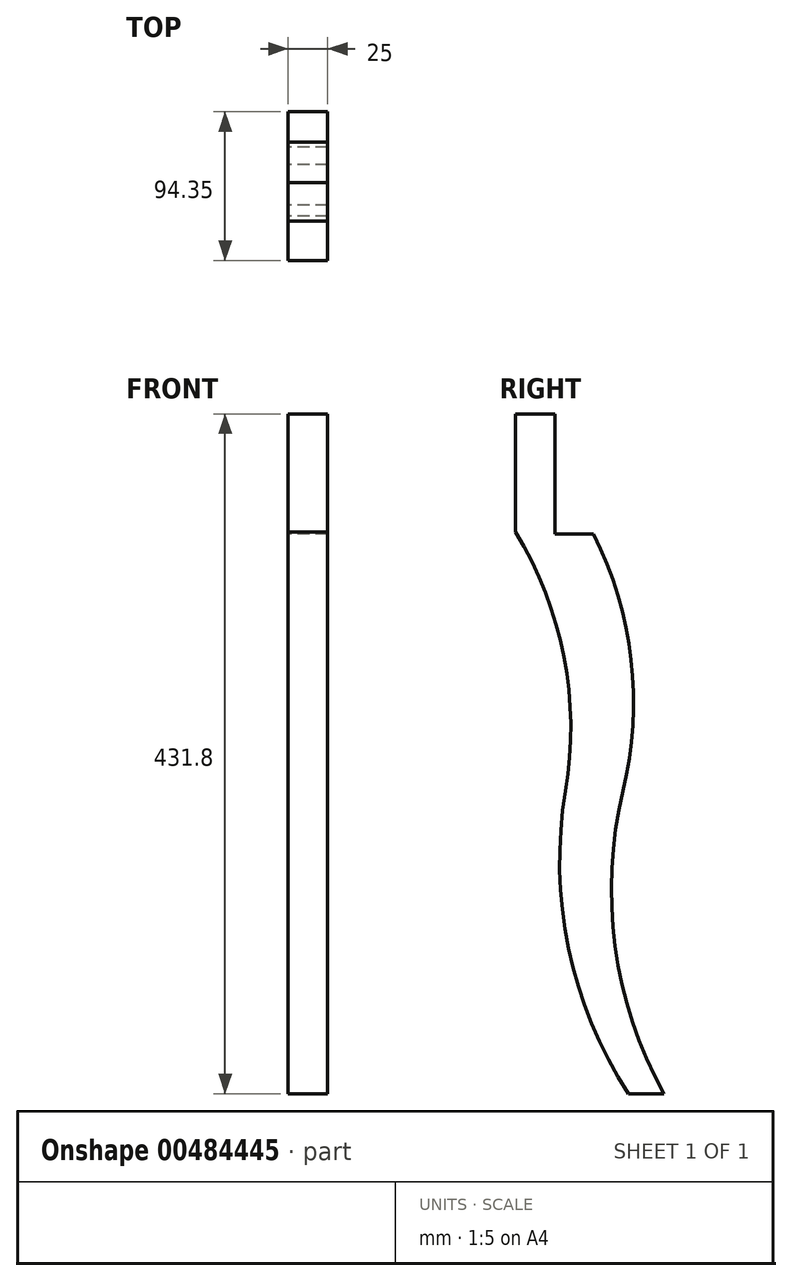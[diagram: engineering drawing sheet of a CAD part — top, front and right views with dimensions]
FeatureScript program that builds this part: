
annotation { "Feature Type Name" : "Feature", "Feature Type Description" : "" }
export const myFeature = defineFeature(function(context is Context, id is Id, definition is map)
    precondition{}
    {
        {
            var Q0;
            Q0=qCreatedBy(makeId("Right.planeOp"),FACE);
            var sketch = newSketch(context, id + "F0", { "sketchPlane" : qUnion([Q0])});
            skLineSegment(sketch, "E0", {"start": v(-61.12, 223.8) * mm, "end": v(-85.62, 223.8) * mm});
            skLineSegment(sketch, "E1", {"start": v(-38.78, -131.8) * mm, "end": v(366.43, -131.8) * mm, "construction": true});
            skLineSegment(sketch, "E2", {"start": v(-256.12, 300) * mm, "end": v(-256.12, -130.22) * mm, "construction": true});
            skLineSegment(sketch, "E3", {"start": v(-85.62, 223.8) * mm, "end": v(-85.62, 300) * mm});
            skLineSegment(sketch, "E4", {"start": v(-85.62, 300) * mm, "end": v(-110.62, 300) * mm});
            skLineSegment(sketch, "E5", {"start": v(-110.62, 300) * mm, "end": v(-110.62, 225) * mm});
            skArc(sketch, "E6", {"start": v(-42.23, 60.54) * mm, "mid": v(-37.16, 143.85) * mm, "end": v(-61.12, 223.8) * mm});
            skArc(sketch, "E7", {"start": v(-42.23, 60.54) * mm, "mid": v(-47.3, -38.07) * mm, "end": v(-16.27, -131.8) * mm});
            skLineSegment(sketch, "E8", {"start": v(-42.23, 60.54) * mm, "end": v(-140.29, 60.54) * mm, "construction": true});
            skArc(sketch, "E9", {"start": v(-78.8, 60.54) * mm, "mid": v(-79.82, 145.65) * mm, "end": v(-110.62, 225) * mm});
            skArc(sketch, "E10", {"start": v(-78.8, 60.54) * mm, "mid": v(-76.9, -39.4) * mm, "end": v(-38.78, -131.8) * mm});
            skLineSegment(sketch, "E11", {"start": v(-38.78, -131.8) * mm, "end": v(-16.27, -131.8) * mm});
            skSolve(sketch);
        }
        {
            var Q0;
            Q0=makeQuery(id+"F0.imprint","IMPRINT",FACE,{"disambiguationData":[TD([[makeQuery(id+"F0.imprint","IMPRINT",EDGE,{"derivedFrom":sQuery(id+"F0.wireOp",EDGE,"E0")}),1.0]])]});
            extrude(context, id + "F1", {"entities" : qUnion([Q0]), "depth" : 25 * mm, "offsetDistance" : 25 * mm});
        }
    });
